# Revit family: P3754-20
name_source: partatom
category: Lighting Fixtures
revit_build: Autodesk Revit MEP 2012 (Build: 20110309_2315(x64)
units: mm (PartAtom-declared; Revit-internal decimal feet)

## types (1)
- P3754-20
    Apparent Load = 0 VA
    Back Plate = Hubbell - Antique Bronze
    Celing chain length = 54.000"
    Default Elevation = 48.000"
    Description = Six-light foyer pendant with clear seeded glass, delicate rope detailing and candle cluster in bowl. Great for entry ways or kitchens.
    Glass = Hubbell - Glass
    Lamp = 60W Candelabra Base
    Load Classification = Lighting
    Manufacturer = Progress Lighting
    Manufacturer Fax = (864)-678-1065
    Model = P3754-20
    Mounting Type = Ceiling Chain Mounted
    Nominal Watts = 60 W
    Product Documentation Link = https://media.progresslighting.com
    Product Page URL = https://progresslighting.com
    URL = https://progresslighting.com
    Voltage = 0 V
    Wattage Comments = 60W

## geometry (parser evidence)
native form markers: Blend x4, Sweep x8
no freeform markers — native parametric forms only
